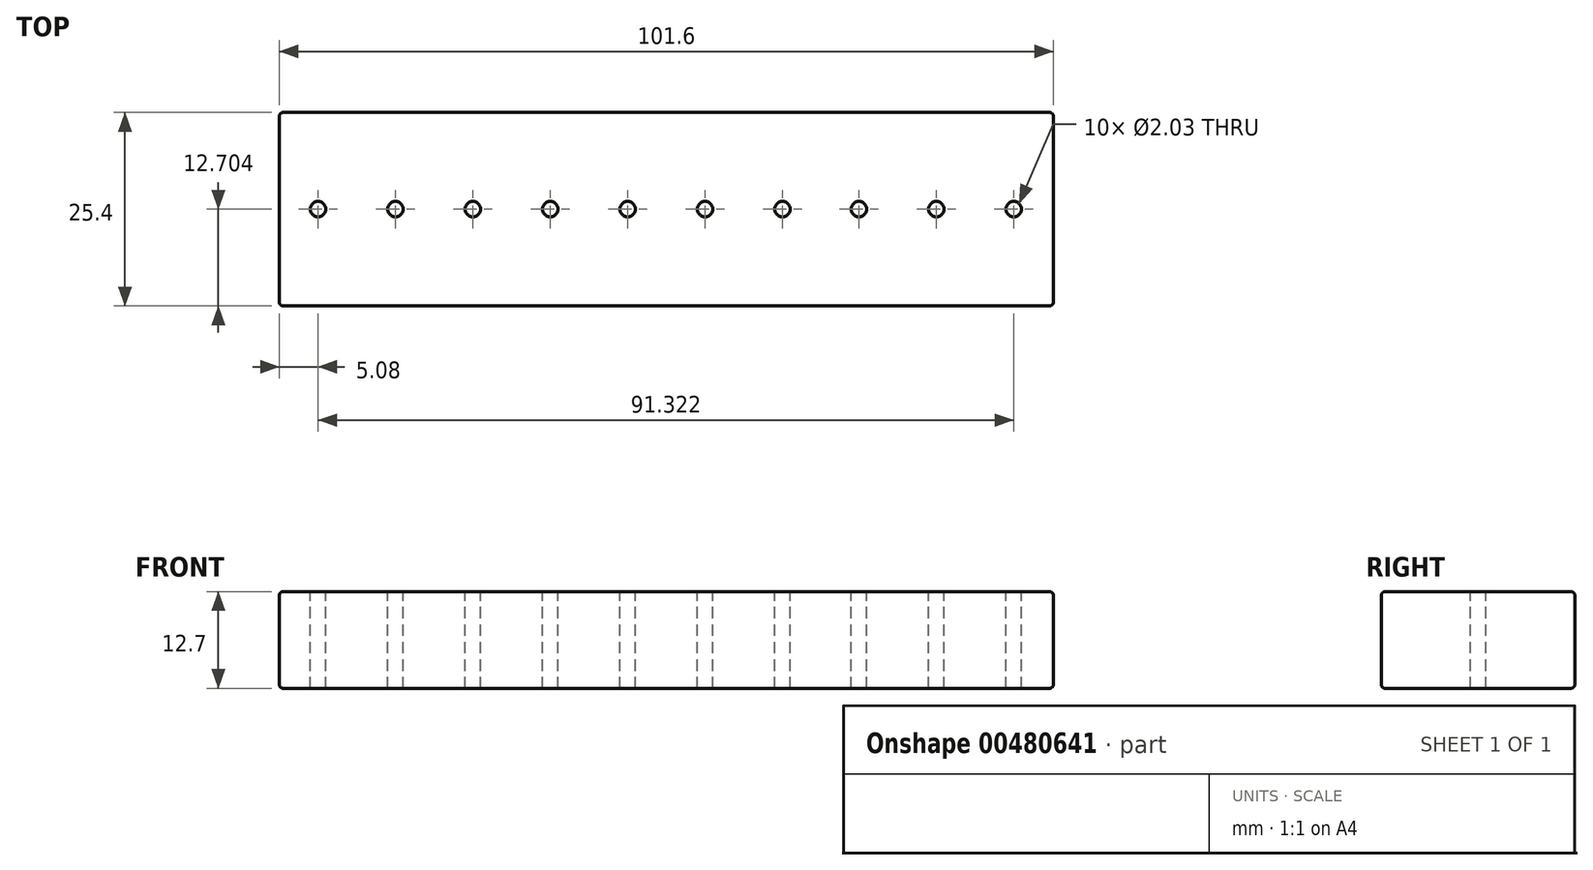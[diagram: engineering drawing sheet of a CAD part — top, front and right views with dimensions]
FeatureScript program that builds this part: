
annotation { "Feature Type Name" : "Feature", "Feature Type Description" : "" }
export const myFeature = defineFeature(function(context is Context, id is Id, definition is map)
    precondition{}
    {
        {
            var Q0;
            Q0=qCreatedBy(makeId("Top.planeOp"),FACE);
            var sketch = newSketch(context, id + "F0", { "sketchPlane" : qUnion([Q0])});
            skLineSegment(sketch, "E0", {"start": v(-61.95, 18.43) * mm, "end": v(39.65, 18.43) * mm});
            skLineSegment(sketch, "E1", {"start": v(39.65, 18.43) * mm, "end": v(39.65, -6.97) * mm});
            skLineSegment(sketch, "E2", {"start": v(39.65, -6.97) * mm, "end": v(-61.95, -6.97) * mm});
            skLineSegment(sketch, "E3", {"start": v(-61.95, -6.97) * mm, "end": v(-61.95, 18.43) * mm});
            skLineSegment(sketch, "E4", {"start": v(-11.15, 18.43) * mm, "end": v(-11.15, -6.97) * mm, "construction": true});
            skLineSegment(sketch, "E5", {"start": v(-11.15, 5.73) * mm, "end": v(-6.07, 5.73) * mm, "construction": true});
            skLineSegment(sketch, "E6", {"start": v(-11.15, 5.73) * mm, "end": v(-16.23, 5.73) * mm, "construction": true});
            skLineSegment(sketch, "E7", {"start": v(-6.07, 5.73) * mm, "end": v(4.09, 5.73) * mm, "construction": true});
            skLineSegment(sketch, "E8", {"start": v(3.97, 5.73) * mm, "end": v(4.09, 5.73) * mm, "construction": true});
            skLineSegment(sketch, "E9", {"start": v(3.97, 5.73) * mm, "end": v(14.13, 5.73) * mm, "construction": true});
            skLineSegment(sketch, "E10", {"start": v(14.13, 5.73) * mm, "end": v(24.3, 5.73) * mm, "construction": true});
            skLineSegment(sketch, "E11", {"start": v(-16.23, 5.73) * mm, "end": v(-26.4, 5.73) * mm, "construction": true});
            skLineSegment(sketch, "E12", {"start": v(-26.4, 5.73) * mm, "end": v(-36.55, 5.73) * mm, "construction": true});
            skLineSegment(sketch, "E13", {"start": v(-36.55, 5.73) * mm, "end": v(-46.71, 5.73) * mm, "construction": true});
            skLineSegment(sketch, "E14", {"start": v(-46.71, 5.73) * mm, "end": v(-56.87, 5.73) * mm, "construction": true});
            skLineSegment(sketch, "E15", {"start": v(24.3, 5.73) * mm, "end": v(34.45, 5.73) * mm, "construction": true});
            skCircle(sketch, "E16", {"center": v(-56.87, 5.73) * mm, "radius": 1.02 * mm});
            skCircle(sketch, "E17", {"center": v(-46.71, 5.73) * mm, "radius": 1.02 * mm});
            skCircle(sketch, "E18", {"center": v(-36.55, 5.73) * mm, "radius": 1.02 * mm});
            skCircle(sketch, "E19", {"center": v(-26.4, 5.73) * mm, "radius": 1.02 * mm});
            skCircle(sketch, "E20", {"center": v(-16.23, 5.73) * mm, "radius": 1.02 * mm});
            skCircle(sketch, "E21", {"center": v(-6.07, 5.73) * mm, "radius": 1.02 * mm});
            skCircle(sketch, "E22", {"center": v(4.09, 5.73) * mm, "radius": 1.02 * mm});
            skCircle(sketch, "E23", {"center": v(14.13, 5.73) * mm, "radius": 1.02 * mm});
            skCircle(sketch, "E24", {"center": v(24.3, 5.73) * mm, "radius": 1.02 * mm});
            skCircle(sketch, "E25", {"center": v(34.45, 5.73) * mm, "radius": 1.02 * mm});
            skSolve(sketch);
        }
        {
            var Q0;
            Q0=makeQuery(id+"F0.imprint","IMPRINT",FACE,{"disambiguationData":[TD([[makeQuery(id+"F0.imprint","IMPRINT",EDGE,{"derivedFrom":sQuery(id+"F0.wireOp",EDGE,"E0")}),-1.0]])]});
            extrude(context, id + "F1", {"entities" : qUnion([Q0]), "oppositeDirection" : true, "depth" : 12.7 * mm});
        }
        {
            var Q0;
            Q0=makeQuery(id+"F1.opExtrude","CAP_EDGE",EDGE,{"disambiguationData":[OSD([sQuery(id+"F0.wireOp",EDGE,"E0")])],"isStart":true});
            var Q1;
            Q1=makeQuery(id+"F1.opExtrude","CAP_EDGE",EDGE,{"disambiguationData":[OSD([sQuery(id+"F0.wireOp",EDGE,"E1")])],"isStart":true});
            var Q2;
            Q2=makeQuery(id+"F1.opExtrude","CAP_EDGE",EDGE,{"disambiguationData":[OSD([sQuery(id+"F0.wireOp",EDGE,"E2")])],"isStart":true});
            var Q3;
            Q3=makeQuery(id+"F1.opExtrude","CAP_EDGE",EDGE,{"disambiguationData":[OSD([sQuery(id+"F0.wireOp",EDGE,"E3")])],"isStart":true});
            var Q4;
            Q4=makeQuery(id+"F1.opExtrude","SWEPT_EDGE",EDGE,{"disambiguationData":[OSD([sQuery(id+"F0.wireOp",EDGE,"E2"),sQuery(id+"F0.wireOp",EDGE,"E3")])]});
            var Q5;
            Q5=makeQuery(id+"F1.opExtrude","SWEPT_EDGE",EDGE,{"disambiguationData":[OSD([sQuery(id+"F0.wireOp",EDGE,"E1"),sQuery(id+"F0.wireOp",EDGE,"E2")])]});
            var Q6;
            Q6=makeQuery(id+"F1.opExtrude","SWEPT_EDGE",EDGE,{"disambiguationData":[OSD([sQuery(id+"F0.wireOp",EDGE,"E0"),sQuery(id+"F0.wireOp",EDGE,"E1")])]});
            var Q7;
            Q7=makeQuery(id+"F1.opExtrude","SWEPT_EDGE",EDGE,{"disambiguationData":[OSD([sQuery(id+"F0.wireOp",EDGE,"E0"),sQuery(id+"F0.wireOp",EDGE,"E3")])]});
            var Q8;
            Q8=makeQuery(id+"F1.opExtrude","CAP_EDGE",EDGE,{"disambiguationData":[OSD([sQuery(id+"F0.wireOp",EDGE,"E1")])],"isStart":false});
            var Q9;
            Q9=makeQuery(id+"F1.opExtrude","CAP_EDGE",EDGE,{"disambiguationData":[OSD([sQuery(id+"F0.wireOp",EDGE,"E0")])],"isStart":false});
            var Q10;
            Q10=makeQuery(id+"F1.opExtrude","CAP_EDGE",EDGE,{"disambiguationData":[OSD([sQuery(id+"F0.wireOp",EDGE,"E3")])],"isStart":false});
            var Q11;
            Q11=makeQuery(id+"F1.opExtrude","CAP_EDGE",EDGE,{"disambiguationData":[OSD([sQuery(id+"F0.wireOp",EDGE,"E2")])],"isStart":false});
            fillet(context, id + "F2", {"entities" : qUnion([Q0, Q1, Q2, Q3, Q4, Q5, Q6, Q7, Q8, Q9, Q10, Q11]), "radius" : 0.5 * mm, "tangentPropagation" : true, "allowEdgeOverflow" : false});
        }
    });
